# Revit family: 1RTD-BR_Bypass_DN15-20_RFA
name_source: partatom
category: Pipe Accessories
units: mm (PartAtom-declared; Revit-internal decimal feet)

## family parameters
Always vertical = Yes
Cut with Voids When Loaded = No
OmniClass Number = 23.65.55.14.17
OmniClass Title = Adjusting/Controlling Valves for Liquid Services
Part Type = Valve - Breaks Into
Round Connector Dimension = Use Diameter
Shared = No
Work Plane-Based = No

## types (2) — shared parameters
Description = Flow Restrictor
IfcExportAs = IfcValveType
IfcExportType = RTD-BR
L = 48 mm
LOD 200 = No
LOD 350 = Yes
Manufacturer = Danfoss
Max Operating Pressure = 10 bar
Max Working Temperature = 120 °C
URL = https://store.danfoss.com
Valve Body Material = Danfoss Cast Steel

## per-type parameters (varying)
| type | D | D1 | Kvs | Model | Model Type | R_200 | S1 | S2 | Weight |
| RTD-BR_Bypass_DN20_15_013L1916 | 20 mm  [stored 0.0656168 ft] | 34 mm | 15.1 m³/h | 013L1916 | RTD-BR_Bypass_DN20_15 | 27 mm  [stored 0.0885827 ft] | 25 mm  [stored 0.082021 ft] | 50 mm  [stored 0.164042 ft] | 0.29 kg |
| RTD-BR_Bypass_DN15_10_013L1915 | 15 mm  [stored 0.0492126 ft] | 31 mm  [stored 0.101706 ft] | 6.8 m³/h | 013L1915 | RTD-BR_Bypass_DN15_10 | 22 mm | 20 mm  [stored 0.0656168 ft] | 40 mm  [stored 0.131234 ft] | 0.17 kg |

note: [stored X ft] marks values corroborated as IEEE doubles in the binary element streams (Revit-internal decimal feet)

## geometry (parser evidence)
native form markers: Sweep x3
no freeform markers — native parametric forms only
